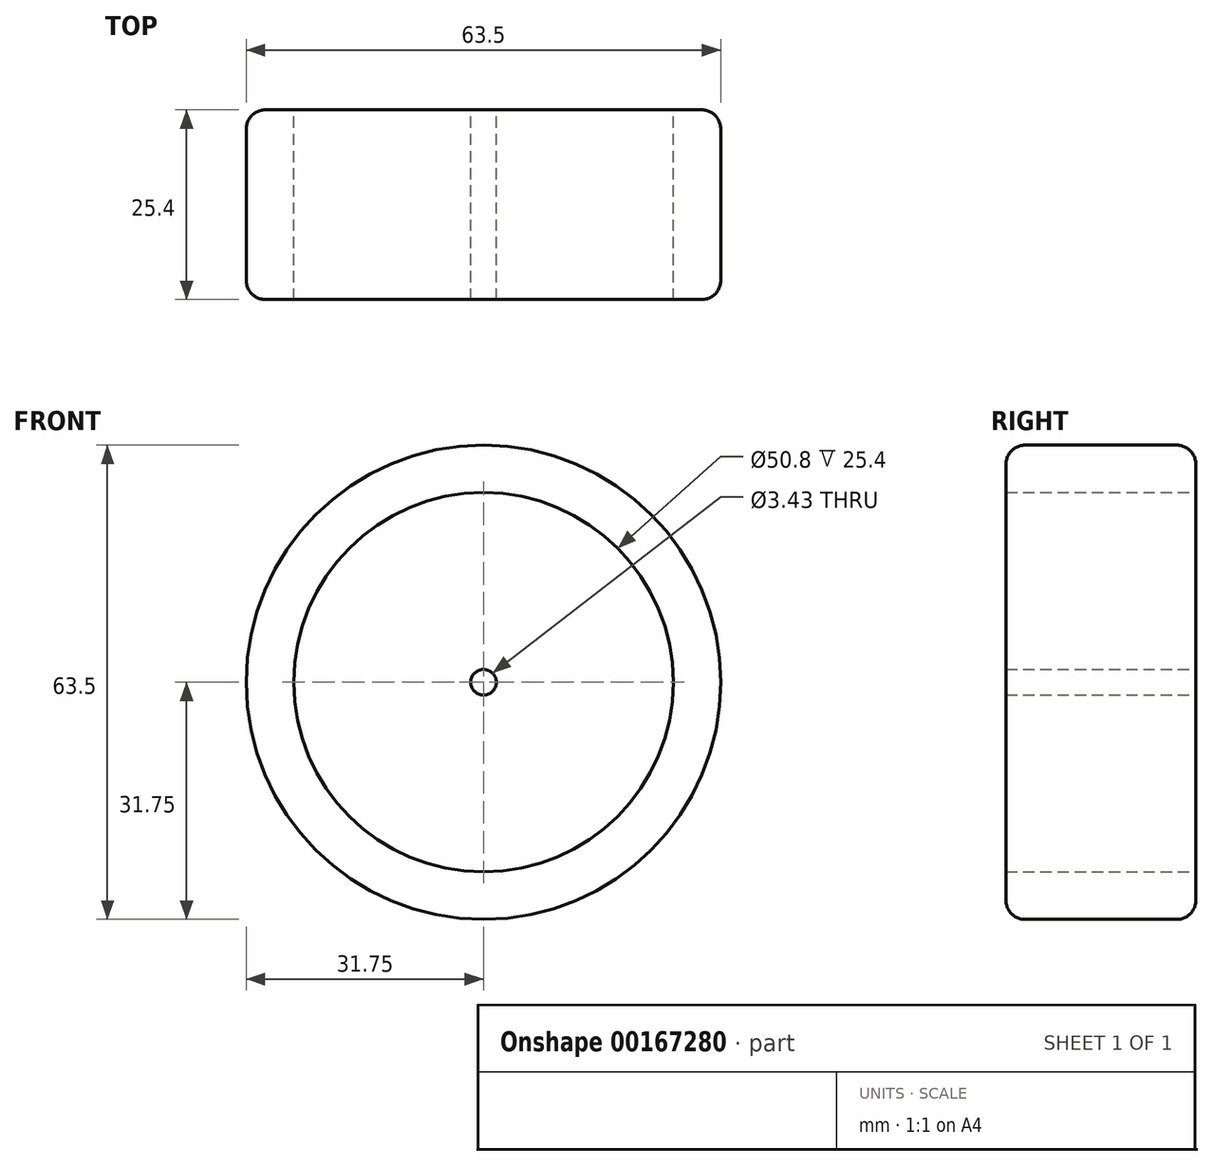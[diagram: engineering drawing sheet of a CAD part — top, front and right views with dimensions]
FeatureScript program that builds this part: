
annotation { "Feature Type Name" : "Feature", "Feature Type Description" : "" }
export const myFeature = defineFeature(function(context is Context, id is Id, definition is map)
    precondition{}
    {
        {
            var Q0;
            Q0=qCreatedBy(makeId("Front.planeOp"),FACE);
            var sketch = newSketch(context, id + "F0", { "sketchPlane" : qUnion([Q0])});
            skCircle(sketch, "E0", {"center": v(0, 0) * mm, "radius": 31.75 * mm});
            skCircle(sketch, "E1.0", {"center": v(0, 0) * mm, "radius": 25.4 * mm});
            skCircle(sketch, "E2", {"center": v(0, 0) * mm, "radius": 1.71 * mm});
            skSolve(sketch);
        }
        {
            var Q0;
            Q0=makeQuery(id+"F0.imprint","IMPRINT",FACE,{"disambiguationData":[TD([[makeQuery(id+"F0.imprint","IMPRINT",EDGE,{"derivedFrom":sQuery(id+"F0.wireOp",EDGE,"E1.0")}),1.0]])]});
            extrude(context, id + "F1", {"entities" : qUnion([Q0]), "depth" : 25.4 * mm});
        }
        {
            var Q0;
            Q0 = qSketchRegion(id + "F0", true);
            extrude(context, id + "F2", {"entities" : qUnion([Q0]), "depth" : 25.4 * mm});
        }
        {
            var Q0;
            Q0=makeQuery(id+"F2.opExtrude","CAP_EDGE",EDGE,{"disambiguationData":[OSD([sQuery(id+"F0.wireOp",EDGE,"E0")])],"isStart":false});
            fillet(context, id + "F3", {"entities" : qUnion([Q0]), "radius" : 2.54 * mm, "tangentPropagation" : true, "allowEdgeOverflow" : false});
        }
        {
            var Q0;
            Q0=makeQuery(id+"F2.opExtrude","CAP_EDGE",EDGE,{"disambiguationData":[OSD([sQuery(id+"F0.wireOp",EDGE,"E0")])],"isStart":true});
            fillet(context, id + "F4", {"entities" : qUnion([Q0]), "radius" : 2.54 * mm, "tangentPropagation" : true, "allowEdgeOverflow" : false});
        }
    });
